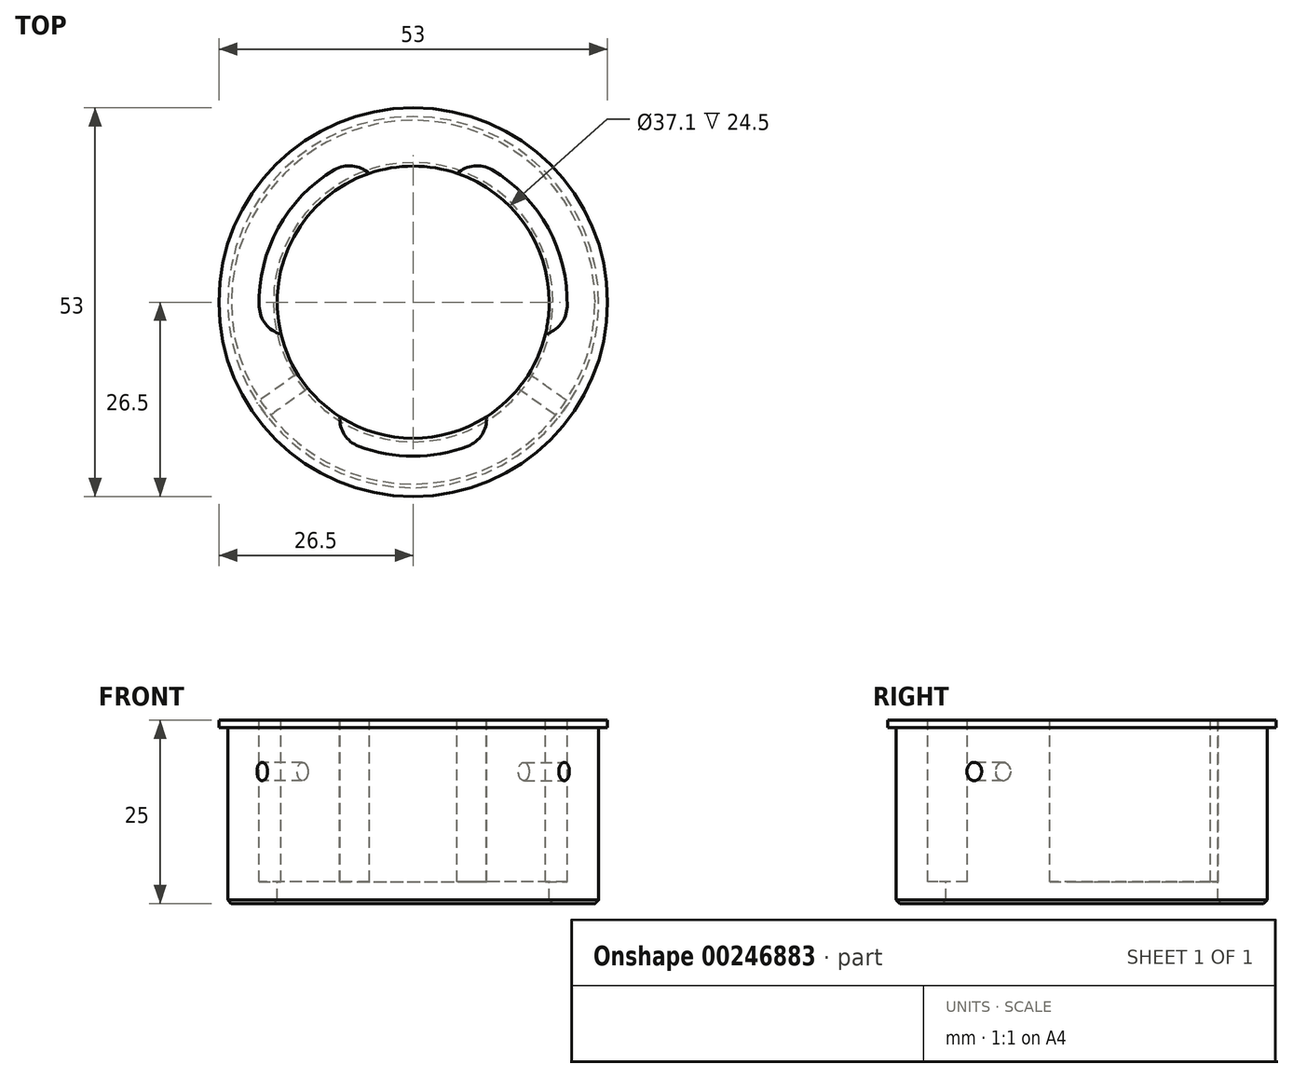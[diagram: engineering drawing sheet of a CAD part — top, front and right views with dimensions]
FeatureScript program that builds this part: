
annotation { "Feature Type Name" : "Feature", "Feature Type Description" : "" }
export const myFeature = defineFeature(function(context is Context, id is Id, definition is map)
    precondition{}
    {
        {
            var Q0;
            Q0=qCreatedBy(makeId("Top.planeOp"),FACE);
            var sketch = newSketch(context, id + "F0", { "sketchPlane" : qUnion([Q0])});
            skLineSegment(sketch, "E0", {"start": v(0, 26.32) * mm, "end": v(0, -30.7) * mm, "construction": true});
            skLineSegment(sketch, "E1", {"start": v(-30.13, 0) * mm, "end": v(28.93, 0) * mm, "construction": true});
            skCircle(sketch, "E2", {"center": v(0, 0) * mm, "radius": 26.5 * mm});
            skCircle(sketch, "E3", {"center": v(0, 0) * mm, "radius": 25.3 * mm});
            skCircle(sketch, "E4", {"center": v(0, 0) * mm, "radius": 18.55 * mm});
            skCircle(sketch, "E5", {"center": v(0, 0) * mm, "radius": 21 * mm});
            skPoint(sketch, "E6", {"position": v(6, 17.55) * mm});
            skPoint(sketch, "E7", {"position": v(18.03, -4.36) * mm});
            skPoint(sketch, "E8", {"position": v(10, -15.62) * mm});
            skLineSegment(sketch, "E9", {"start": v(6, 17.55) * mm, "end": v(6.8, 19.87) * mm});
            skLineSegment(sketch, "E10", {"start": v(18.03, -4.36) * mm, "end": v(20.41, -4.94) * mm});
            skLineSegment(sketch, "E11", {"start": v(10, -15.62) * mm, "end": v(11.32, -17.69) * mm});
            skLineSegment(sketch, "E12", {"start": v(0, 0) * mm, "end": v(33.62, -23.97) * mm, "construction": true});
            skLineSegment(sketch, "E13.MirrorCS", {"start": v(0, 0) * mm, "end": v(-33.62, -23.97) * mm, "construction": true});
            skLineSegment(sketch, "E14.MirrorCS", {"start": v(-10, -15.62) * mm, "end": v(-11.32, -17.69) * mm});
            skLineSegment(sketch, "E15.MirrorCS", {"start": v(-18.03, -4.36) * mm, "end": v(-20.41, -4.94) * mm});
            skLineSegment(sketch, "E16.MirrorCS", {"start": v(-6, 17.55) * mm, "end": v(-6.8, 19.87) * mm});
            skPoint(sketch, "E17", {"position": v(-21.58, -15.39) * mm});
            skPoint(sketch, "E18", {"position": v(21.58, -15.39) * mm});
            skSolve(sketch);
        }
        {
            var Q0;
            Q0=makeQuery(id+"F0.imprint","IMPRINT",FACE,{"disambiguationData":[TD([[makeQuery(id+"F0.imprint","IMPRINT",EDGE,{"derivedFrom":sQuery(id+"F0.wireOp",EDGE,"E2")}),1.0]])]});
            var Q1;
            Q1=makeQuery(id+"F0.imprint","IMPRINT",FACE,{"disambiguationData":[TD([[makeQuery(id+"F0.imprint","IMPRINT",EDGE,{"derivedFrom":sQuery(id+"F0.wireOp",EDGE,"E3")}),1.0]])]});
            extrude(context, id + "F1", {"entities" : qUnion([Q0, Q1]), "oppositeDirection" : true, "depth" : 1 * mm});
        }
        {
            var Q0;
            Q0=makeQuery(id+"F0.imprint","IMPRINT",FACE,{"disambiguationData":[TD([[makeQuery(id+"F0.imprint","IMPRINT",EDGE,{"derivedFrom":sQuery(id+"F0.wireOp",EDGE,"E3")}),1.0]])]});
            var Q1;
            {var subQ0=sQuery(id+"F0.wireOp",EDGE,"E10");Q1=makeQuery(id+"F0.imprint","IMPRINT",FACE,{"disambiguationData":[TD([[makeQuery(id+"F0.imprint","IMPRINT",EDGE,{"derivedFrom":subQ0}),-1.0]])]});}
            var Q2;
            {var subQ0=sQuery(id+"F0.wireOp",EDGE,"E9");Q2=makeQuery(id+"F0.imprint","IMPRINT",FACE,{"disambiguationData":[TD([[makeQuery(id+"F0.imprint","IMPRINT",EDGE,{"derivedFrom":subQ0}),-1.0]])]});}
            var Q3;
            {var subQ0=sQuery(id+"F0.wireOp",EDGE,"E9");Q3=makeQuery(id+"F0.imprint","IMPRINT",FACE,{"disambiguationData":[TD([[makeQuery(id+"F0.imprint","IMPRINT",EDGE,{"derivedFrom":subQ0}),1.0]])]});}
            var Q4;
            {var subQ0=sQuery(id+"F0.wireOp",EDGE,"E15.MirrorCS");Q4=makeQuery(id+"F0.imprint","IMPRINT",FACE,{"disambiguationData":[TD([[makeQuery(id+"F0.imprint","IMPRINT",EDGE,{"derivedFrom":subQ0}),-1.0]])]});}
            var Q5;
            {var subQ0=sQuery(id+"F0.wireOp",EDGE,"E14.MirrorCS");Q5=makeQuery(id+"F0.imprint","IMPRINT",FACE,{"disambiguationData":[TD([[makeQuery(id+"F0.imprint","IMPRINT",EDGE,{"derivedFrom":subQ0}),-1.0]])]});}
            var Q6;
            {var subQ0=sQuery(id+"F0.wireOp",EDGE,"E11");Q6=makeQuery(id+"F0.imprint","IMPRINT",FACE,{"disambiguationData":[TD([[makeQuery(id+"F0.imprint","IMPRINT",EDGE,{"derivedFrom":subQ0}),-1.0]])]});}
            extrude(context, id + "F2", {"entities" : qUnion([Q0, Q1, Q2, Q3, Q4, Q5, Q6]), "operationType" : NewBodyOperationType.ADD, "oppositeDirection" : true, "depth" : 25 * mm});
        }
        {
            var Q0;
            {var subQ0=sQuery(id+"F0.wireOp",EDGE,"E9");Q0=makeQuery(id+"F0.imprint","IMPRINT",FACE,{"disambiguationData":[TD([[makeQuery(id+"F0.imprint","IMPRINT",EDGE,{"derivedFrom":subQ0}),-1.0]])]});}
            var Q1;
            {var subQ0=sQuery(id+"F0.wireOp",EDGE,"E11");Q1=makeQuery(id+"F0.imprint","IMPRINT",FACE,{"disambiguationData":[TD([[makeQuery(id+"F0.imprint","IMPRINT",EDGE,{"derivedFrom":subQ0}),-1.0]])]});}
            var Q2;
            {var subQ0=sQuery(id+"F0.wireOp",EDGE,"E15.MirrorCS");Q2=makeQuery(id+"F0.imprint","IMPRINT",FACE,{"disambiguationData":[TD([[makeQuery(id+"F0.imprint","IMPRINT",EDGE,{"derivedFrom":subQ0}),-1.0]])]});}
            extrude(context, id + "F3", {"entities" : qUnion([Q0, Q1, Q2]), "operationType" : NewBodyOperationType.REMOVE, "oppositeDirection" : true, "depth" : 22 * mm});
        }
        {
            var Q0;
            Q0=makeQuery(id+"F3.boolean.opBoolean","COPY",EDGE,{"derivedFrom":makeQuery(id+"F3.opExtrude","SWEPT_EDGE",EDGE,{"disambiguationData":[OSD([sQuery(id+"F0.wireOp",EDGE,"E5"),sQuery(id+"F0.wireOp",EDGE,"E9")])]})});
            var Q1;
            Q1=makeQuery(id+"F3.boolean.opBoolean","COPY",EDGE,{"derivedFrom":makeQuery(id+"F3.opExtrude","SWEPT_EDGE",EDGE,{"disambiguationData":[OSD([sQuery(id+"F0.wireOp",EDGE,"E5"),sQuery(id+"F0.wireOp",EDGE,"E16.MirrorCS")])]})});
            var Q2;
            Q2=makeQuery(id+"F3.boolean.opBoolean","COPY",EDGE,{"derivedFrom":makeQuery(id+"F3.opExtrude","SWEPT_EDGE",EDGE,{"disambiguationData":[OSD([sQuery(id+"F0.wireOp",EDGE,"E5"),sQuery(id+"F0.wireOp",EDGE,"E10")])]})});
            var Q3;
            Q3=makeQuery(id+"F3.boolean.opBoolean","COPY",EDGE,{"derivedFrom":makeQuery(id+"F3.opExtrude","SWEPT_EDGE",EDGE,{"disambiguationData":[OSD([sQuery(id+"F0.wireOp",EDGE,"E5"),sQuery(id+"F0.wireOp",EDGE,"E11")])]})});
            var Q4;
            Q4=makeQuery(id+"F3.boolean.opBoolean","COPY",EDGE,{"derivedFrom":makeQuery(id+"F3.opExtrude","SWEPT_EDGE",EDGE,{"disambiguationData":[OSD([sQuery(id+"F0.wireOp",EDGE,"E5"),sQuery(id+"F0.wireOp",EDGE,"E14.MirrorCS")])]})});
            var Q5;
            Q5=makeQuery(id+"F3.boolean.opBoolean","COPY",EDGE,{"derivedFrom":makeQuery(id+"F3.opExtrude","SWEPT_EDGE",EDGE,{"disambiguationData":[OSD([sQuery(id+"F0.wireOp",EDGE,"E5"),sQuery(id+"F0.wireOp",EDGE,"E15.MirrorCS")])]})});
            fillet(context, id + "F4", {"entities" : qUnion([Q0, Q1, Q2, Q3, Q4, Q5]), "radius" : 4 * mm, "tangentPropagation" : true, "allowEdgeOverflow" : false});
        }
        {
            var Q0;
            Q0=sQuery(id+"F0.wireOp",VERTEX,"E18");
            var Q1;
            Q1=sQuery(id+"F0.wireOp",EDGE,"E12");
            cPlane(context, id + "F5", {"entities" : qUnion([Q0, Q1]), "cplaneType" : CPlaneType.LINE_POINT, "offset" : 25 * mm, "width" : 150 * mm, "height" : 150 * mm});
        }
        {
            var Q0;
            Q0=sQuery(id+"F0.wireOp",VERTEX,"E17");
            var Q1;
            Q1=sQuery(id+"F0.wireOp",EDGE,"E13.MirrorCS");
            cPlane(context, id + "F6", {"entities" : qUnion([Q0, Q1]), "cplaneType" : CPlaneType.LINE_POINT, "offset" : 25 * mm, "width" : 150 * mm, "height" : 150 * mm});
        }
        {
            var Q0;
            Q0=qCreatedBy(id+"F5.planeOp",FACE);
            var sketch = newSketch(context, id + "F7", { "sketchPlane" : qUnion([Q0])});
            skLineSegment(sketch, "E19", {"start": v(0, -1) * mm, "end": v(0, 0) * mm});
            skPoint(sketch, "E20", {"position": v(0, -7) * mm});
            skSolve(sketch);
        }
        {
            var Q0;
            Q0=qCreatedBy(id+"F6.planeOp",FACE);
            var sketch = newSketch(context, id + "F8", { "sketchPlane" : qUnion([Q0])});
            skLineSegment(sketch, "E21", {"start": v(0, -1) * mm, "end": v(0, 0) * mm});
            skPoint(sketch, "E22", {"position": v(0, -7) * mm});
            skPoint(sketch, "E22.positionSnap0", {"position": v(0, -0.5) * mm});
            skSolve(sketch);
        }
        {
            var Q0;
            Q0=sQuery(id+"F8.wireOp",VERTEX,"E22");
            var Q1;
            Q1=sQuery(id+"F7.wireOp",VERTEX,"E20");
            var Q2;
            Q2=makeQuery(id+"F1.opExtrude","SWEPT_BODY",BODY,{"disambiguationData":[OSD([sQuery(id+"F0.wireOp",EDGE,"E2"),sQuery(id+"F0.wireOp",EDGE,"E5")])]});
            hole(context, id + "F9", {"style" : HoleStyle.SIMPLE, "endStyle" : HoleEndStyle.BLIND, "standardTappedOrClearance" : lookupTablePath({ "standard" : "ISO", "engagement" : "75%", "pitch" : "0.5 mm", "size" : "M3", "type" : "Tapped" }), "standardBlindInLast" : lookupTablePath({ "standard" : "ISO", "engagement" : "75%", "pitch" : "0.5 mm", "size" : "M3", "type" : "Tapped" }), "holeDiameter" : 2.5 * mm, "showTappedDepth" : true, "holeDepth" : 25 * mm, "isTappedThrough" : true, "tappedDepth" : 23.5 * mm, "tapClearance" : 3, "locations" : qUnion([Q0, Q1]), "scope" : qUnion([Q2]), "majorDiameter" : 3 * mm});
        }
        {
            var Q0;
            Q0=makeQuery(id+"F2.opExtrude","CAP_EDGE",EDGE,{"disambiguationData":[OSD([sQuery(id+"F0.wireOp",EDGE,"E4")])],"isStart":false});
            var Q1;
            Q1=makeQuery(id+"F2.opExtrude","CAP_EDGE",EDGE,{"disambiguationData":[OSD([sQuery(id+"F0.wireOp",EDGE,"E3")])],"isStart":false});
            chamfer(context, id + "F10", {"entities" : qUnion([Q0, Q1]), "width" : 0.5 * mm, "tangentPropagation" : true});
        }
    });
